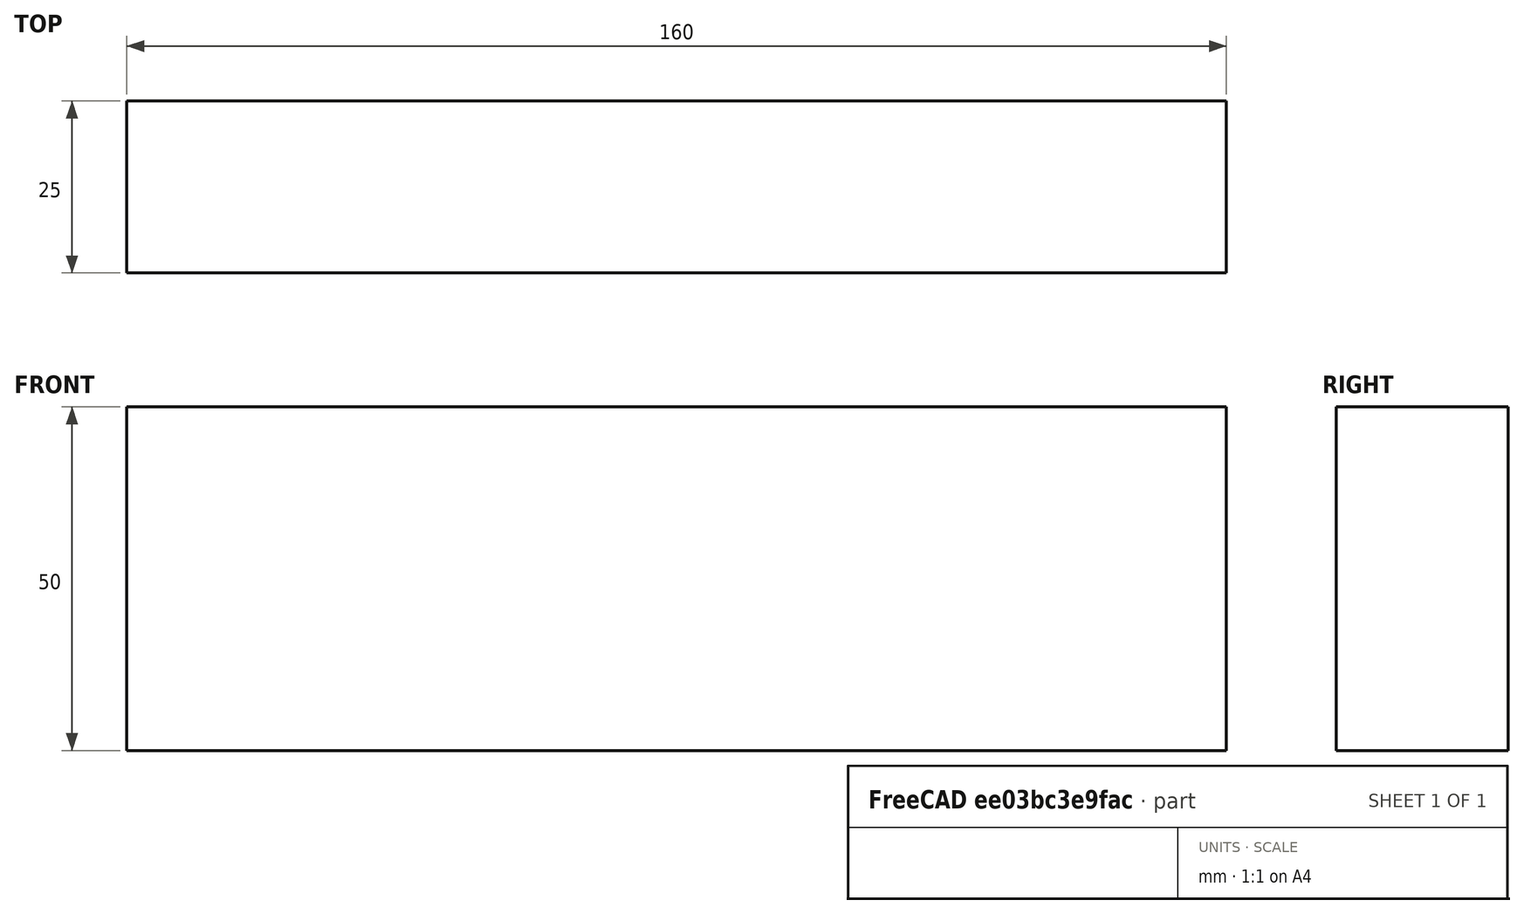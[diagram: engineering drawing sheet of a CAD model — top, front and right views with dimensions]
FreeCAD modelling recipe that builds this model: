
FCSTD DOCUMENT  (FreeCAD 0.15R4671 (Git))
Label: Flat Bar 160x25 EN10058 S235JR
License: All rights reserved
LicenseURL: http://en.wikipedia.org/wiki/All_rights_reserved
objects: Sketcher::SketchObject×1, Part::Extrusion×1
note: 2 computed .brp shape members not serialized (recipe doc carries the construction recipe); baked Part::Feature solids carry a one-line shape summary decoded from their .brp

FEATURE [Sketcher::SketchObject] Sketch
  sketch-geometry (4):
    g0: LineSegment StartX=-80 StartY=-12.5 StartZ=0 EndX=80 EndY=-12.5 EndZ=0
    g1: LineSegment StartX=80 StartY=-12.5 StartZ=0 EndX=80 EndY=12.5 EndZ=0
    g2: LineSegment StartX=80 StartY=12.5 StartZ=0 EndX=-80 EndY=12.5 EndZ=0
    g3: LineSegment StartX=-80 StartY=12.5 StartZ=0 EndX=-80 EndY=-12.5 EndZ=0
  constraints (12):
    c: Coincident(g0,g1)
    c: Coincident(g1,g2)
    c: Coincident(g2,g3)
    c: Coincident(g3,g0)
    c: Horizontal(g0)
    c: Horizontal(g2)
    c: Vertical(g1)
    c: Vertical(g3)
    c: Symmetric(g1,g2,g-2)
    c: Symmetric(g0,g1,g-1)
    c: DistanceY(g1) = 25
    c: DistanceX(g0) = 160
FEATURE [Part::Extrusion] Extrude  label="Flat Bar 160x25 EN10058 S235JR"
  Base = -> Sketch
  Dir = (0,0,50)
  Solid = true
